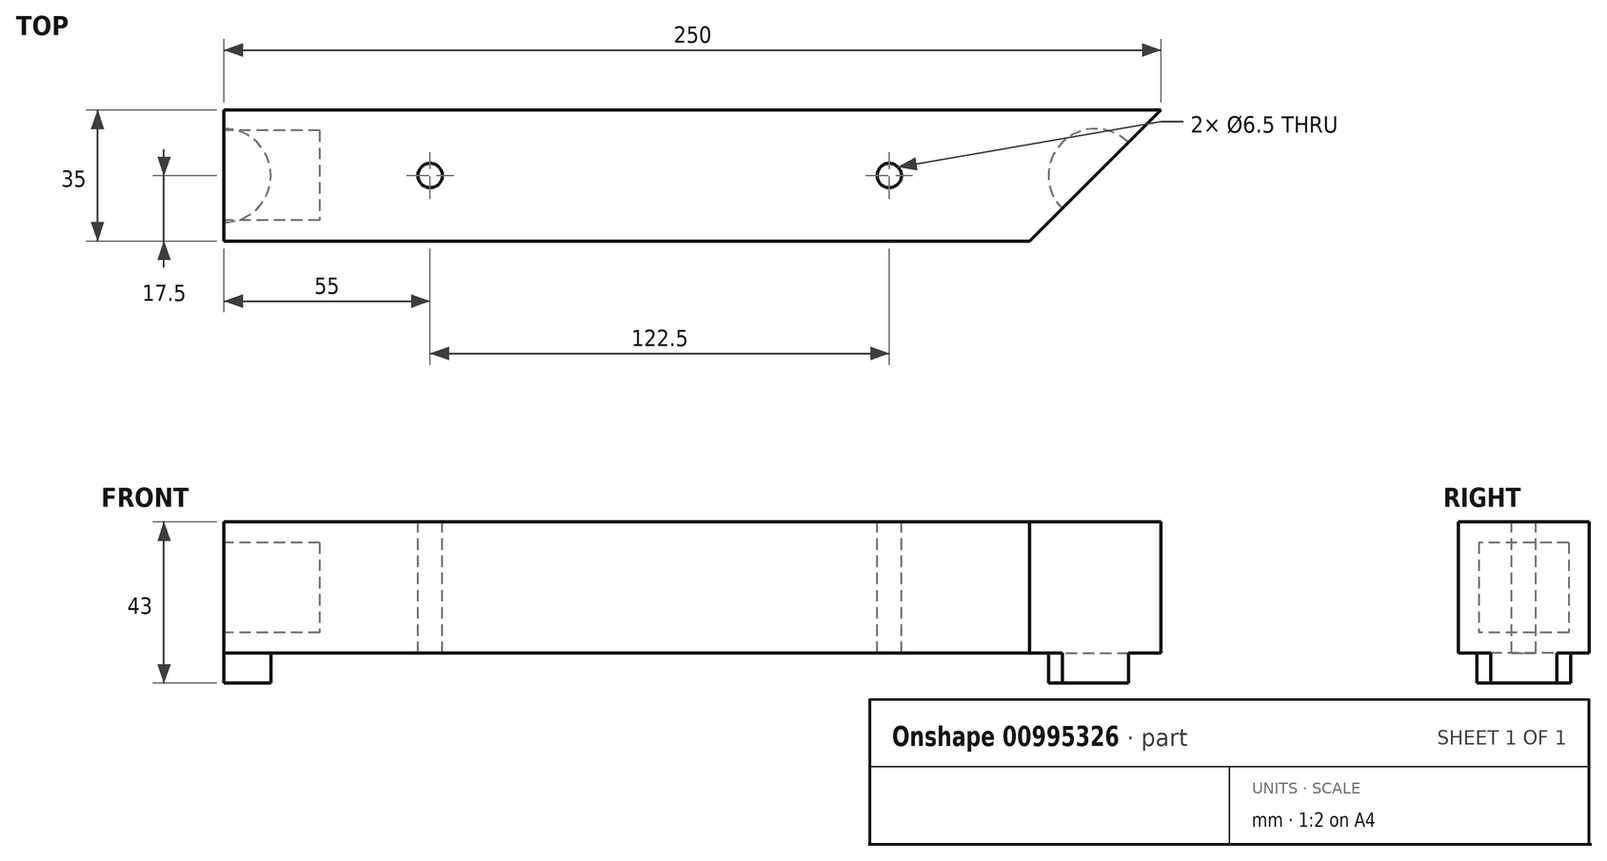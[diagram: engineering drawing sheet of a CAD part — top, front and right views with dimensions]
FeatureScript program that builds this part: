
annotation { "Feature Type Name" : "Feature", "Feature Type Description" : "" }
export const myFeature = defineFeature(function(context is Context, id is Id, definition is map)
    precondition{}
    {
        {
            var Q0;
            Q0=qCreatedBy(makeId("Top.planeOp"),FACE);
            var sketch = newSketch(context, id + "F0", { "sketchPlane" : qUnion([Q0])});
            skLineSegment(sketch, "E0.bottom", {"start": v(125, 17.5) * mm, "end": v(-125, 17.5) * mm});
            skLineSegment(sketch, "E0.top", {"start": v(90, -17.5) * mm, "end": v(-125, -17.5) * mm});
            skLineSegment(sketch, "E0.right", {"start": v(-125, 17.5) * mm, "end": v(-125, -17.5) * mm});
            skPoint(sketch, "E0.middle", {"position": v(0, 0) * mm});
            skPoint(sketch, "E1", {"position": v(90, -17.5) * mm});
            skLineSegment(sketch, "E2", {"start": v(125, 17.5) * mm, "end": v(90, -17.5) * mm});
            skPoint(sketch, "E3.orphan", {"position": v(125, -17.5) * mm});
            skSolve(sketch);
        }
        {
            var Q0;
            Q0=makeQuery(id+"F0.imprint","IMPRINT",FACE,{"disambiguationData":[TD([[makeQuery(id+"F0.imprint","IMPRINT",EDGE,{"derivedFrom":sQuery(id+"F0.wireOp",EDGE,"E0.bottom")}),1.0]])]});
            extrude(context, id + "F1", {"entities" : qUnion([Q0]), "depth" : 35 * mm, "offsetDistance" : 25 * mm});
        }
        {
            var Q0;
            Q0=makeQuery(id+"F1.opExtrude","CAP_FACE",FACE,{"disambiguationData":[OSD([sQuery(id+"F0.wireOp",EDGE,"E0.bottom"),sQuery(id+"F0.wireOp",EDGE,"E0.top"),sQuery(id+"F0.wireOp",EDGE,"E0.right"),sQuery(id+"F0.wireOp",EDGE,"E2")])],"isStart":false});
            var sketch = newSketch(context, id + "F2", { "sketchPlane" : qUnion([Q0])});
            skPoint(sketch, "E4", {"position": v(52.5, 0) * mm});
            skPoint(sketch, "E5", {"position": v(107.5, 0) * mm});
            skPoint(sketch, "E6", {"position": v(-70, 0) * mm});
            skPoint(sketch, "E7", {"position": v(-125, 0) * mm});
            skSolve(sketch);
        }
        {
            var Q0;
            Q0=sQuery(id+"F2.wireOp",VERTEX,"E6");
            var Q1;
            Q1=makeQuery(id+"F1.opExtrude","SWEPT_BODY",BODY,{"disambiguationData":[OSD([sQuery(id+"F0.wireOp",EDGE,"E0.bottom"),sQuery(id+"F0.wireOp",EDGE,"E0.top"),sQuery(id+"F0.wireOp",EDGE,"E0.right"),sQuery(id+"F0.wireOp",EDGE,"E2")])]});
            hole(context, id + "F3", {"style" : HoleStyle.SIMPLE, "endStyle" : HoleEndStyle.BLIND, "holeDiameter" : 6.5 * mm, "majorDiameter" : 5 * mm, "holeDepth" : 35 * mm, "isTappedThrough" : true, "tappedDepth" : 12 * mm, "tapClearance" : 3, "locations" : qUnion([Q0]), "scope" : qUnion([Q1])});
        }
        {
            var Q0;
            Q0=sQuery(id+"F2.wireOp",VERTEX,"E4");
            var Q1;
            Q1=makeQuery(id+"F1.opExtrude","SWEPT_BODY",BODY,{"disambiguationData":[OSD([sQuery(id+"F0.wireOp",EDGE,"E0.bottom"),sQuery(id+"F0.wireOp",EDGE,"E0.top"),sQuery(id+"F0.wireOp",EDGE,"E0.right"),sQuery(id+"F0.wireOp",EDGE,"E2")])]});
            hole(context, id + "F4", {"style" : HoleStyle.SIMPLE, "endStyle" : HoleEndStyle.BLIND, "holeDiameter" : 6.5 * mm, "majorDiameter" : 5 * mm, "holeDepth" : 35 * mm, "isTappedThrough" : true, "tappedDepth" : 12 * mm, "tapClearance" : 3, "locations" : qUnion([Q0]), "scope" : qUnion([Q1])});
        }
        {
            var Q0;
            Q0=makeQuery(id+"F1.opExtrude","SWEPT_FACE",FACE,{"disambiguationData":[OSD([sQuery(id+"F0.wireOp",EDGE,"E0.right")])]});
            var sketch = newSketch(context, id + "F5", { "sketchPlane" : qUnion([Q0])});
            skSolve(sketch);
        }
        {
            var Q0;
            {var subQ0=sQuery(id+"F0.wireOp",EDGE,"E0.right");Q0=makeQuery(id+"F5.imprint","IMPRINT",FACE,{"disambiguationData":[TD([[makeQuery(id+"F5.imprint","IMPRINT",EDGE,{"derivedFrom":makeQuery(id+"F1.opExtrude","CAP_EDGE",EDGE,{"disambiguationData":[OSD([subQ0])],"isStart":true})}),1.0]])]});}
            var sketch = newSketch(context, id + "F6", { "sketchPlane" : qUnion([Q0])});
            skLineSegment(sketch, "E8.0", {"start": v(-12, 5.5) * mm, "end": v(12, 5.5) * mm});
            skLineSegment(sketch, "E8.1", {"start": v(-12, 29.5) * mm, "end": v(-12, 5.5) * mm});
            skLineSegment(sketch, "E9.0", {"start": v(12, 29.5) * mm, "end": v(12, 5.5) * mm});
            skLineSegment(sketch, "E9.1", {"start": v(-12, 29.5) * mm, "end": v(12, 29.5) * mm});
            skSolve(sketch);
        }
        {
            var Q0;
            Q0=makeQuery(id+"F6.imprint","IMPRINT",FACE,{"disambiguationData":[TD([[makeQuery(id+"F6.imprint","IMPRINT",EDGE,{"derivedFrom":sQuery(id+"F6.wireOp",EDGE,"E8.0")}),1.0]])]});
            extrude(context, id + "F7", {"entities" : qUnion([Q0]), "operationType" : NewBodyOperationType.REMOVE, "oppositeDirection" : true, "depth" : 25.5 * mm, "offsetDistance" : 25 * mm});
        }
        {
            var Q0;
            Q0=makeQuery(id+"F1.opExtrude","CAP_FACE",FACE,{"disambiguationData":[OSD([sQuery(id+"F0.wireOp",EDGE,"E0.bottom"),sQuery(id+"F0.wireOp",EDGE,"E0.top"),sQuery(id+"F0.wireOp",EDGE,"E0.right"),sQuery(id+"F0.wireOp",EDGE,"E2")])],"isStart":true});
            var sketch = newSketch(context, id + "F8", { "sketchPlane" : qUnion([Q0])});
            skPoint(sketch, "E10", {"position": v(107.5, 0) * mm});
            skCircle(sketch, "E11", {"center": v(107.5, 0) * mm, "radius": 12.5 * mm});
            skSolve(sketch);
        }
        {
            var Q0;
            {var subQ0=sQuery(id+"F8.wireOp",EDGE,"E11");var subQ1=makeQuery(id+"F1.opExtrude","CAP_EDGE",EDGE,{"disambiguationData":[OSD([sQuery(id+"F0.wireOp",EDGE,"E2")])],"isStart":true});var subQ2=makeQuery(id+"F8.imprint","INTERSECT",VERTEX,{"disambiguationData":[OD(0.0)],"derivedFrom":[subQ1,subQ0]});Q0=makeQuery(id+"F8.imprint","IMPRINT",FACE,{"disambiguationData":[TD([[makeQuery(id+"F8.imprint","IMPRINT",EDGE,{"disambiguationData":[TD([[subQ2,1.0]])],"derivedFrom":subQ0}),1.0]])]});}
            extrude(context, id + "F9", {"entities" : qUnion([Q0]), "operationType" : NewBodyOperationType.ADD, "depth" : 8 * mm, "offsetDistance" : 25 * mm});
        }
        {
            var Q0;
            Q0=makeQuery(id+"F1.opExtrude","CAP_FACE",FACE,{"disambiguationData":[OSD([sQuery(id+"F0.wireOp",EDGE,"E0.bottom"),sQuery(id+"F0.wireOp",EDGE,"E0.top"),sQuery(id+"F0.wireOp",EDGE,"E0.right"),sQuery(id+"F0.wireOp",EDGE,"E2")])],"isStart":true});
            var sketch = newSketch(context, id + "F10", { "sketchPlane" : qUnion([Q0])});
            skCircle(sketch, "E12", {"center": v(-125, 0) * mm, "radius": 12.5 * mm});
            skSolve(sketch);
        }
        {
            var Q0;
            {var subQ0=sQuery(id+"F10.wireOp",EDGE,"E12");var subQ1=makeQuery(id+"F1.opExtrude","CAP_EDGE",EDGE,{"disambiguationData":[OSD([sQuery(id+"F0.wireOp",EDGE,"E0.right")])],"isStart":true});var subQ2=makeQuery(id+"F10.imprint","INTERSECT",VERTEX,{"disambiguationData":[OD(0.0)],"derivedFrom":[subQ1,subQ0]});Q0=makeQuery(id+"F10.imprint","IMPRINT",FACE,{"disambiguationData":[TD([[makeQuery(id+"F10.imprint","IMPRINT",EDGE,{"disambiguationData":[TD([[subQ2,-1.0]])],"derivedFrom":subQ0}),1.0]])]});}
            extrude(context, id + "F11", {"entities" : qUnion([Q0]), "operationType" : NewBodyOperationType.ADD, "depth" : 8 * mm, "offsetDistance" : 25 * mm});
        }
    });
